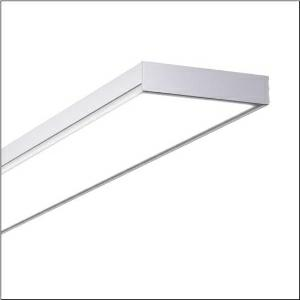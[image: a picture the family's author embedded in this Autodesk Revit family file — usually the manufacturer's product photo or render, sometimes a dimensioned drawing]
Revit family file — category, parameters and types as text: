
# Revit family: apollon_r__31_51mp25wd2341e_bc28
name_source: partatom
category: Lighting Fixtures
units: mm (PartAtom-declared; Revit-internal decimal feet)

## family parameters
Cut with Voids When Loaded = No
Host = Face
Light Source = No
Part Type = Normal
Room Calculation Point = No
Round Connector Dimension = Use Diameter
Shared = No

## types (1)
- Apollon® 31 (1 x LED, 3600 lm, 28 W, 3000K)
    Apparent Load = 28 VA
    CIE Flux Codes = 61 87 97 97 100
    Color Rendering = 80
    Color Temperature = 3000K
    Default Elevation = 1800 mm
    Description = Apollon® 31, office luminaire, primary optical cover: micro prismatic cover, of PMMA, light emission: direct distribution, primary light characteristic: symmetric, installation type: surface-mounted, LED, rated luminous flux: 3.600lm, luminous efficacy: 128lm/W, light colour: 830, colour temperature: 3000K, control gear: ECG DALI, with terminal, 5-pole, mains connection: 220..240V, AC, 50/60Hz, rated input power: 28W, housing, of sheet steel, coil coated, metallic grey (RAL 9006), length: 1.245mm, width: 200mm, height: 44mm, protection rating (complete): IP20, insulation class (complete): insulation class II (safety insulation), certification: CE, impact resistance: IK02, permissible operating ambient temperature: -20..+40°C, standard: EN 60598-2-22, packaging unit: 1 piece
    Height = 44 mm
    Lamp = 1 x LED
    Lamp Light Flux = 3600 lm
    Lamp Power = 28 W
    Lamp count = 1
    Length = 1245 mm
    Luminous efficacy = 129 lm/W
    Manufacturer = Siteco
    ModVariant = No
    Model = 51MP25WD2341E
    Mounting Place = Ceiling
    Mounting Type = Surface mounted
    Number of Poles = 1
    OnlyDefault = Yes
    Power Factor = 1
    Product Name = Apollon® 31
    Product group = office luminaire | ceiling mounted
    ProductGroupID = 302
    Protection Class = Protection class II
    Protection Degree = IP 20
    RLX_Detail_Level = 1
    RlxData = <blob elided: 24081 chars, md5=c3f55dd4>
    Socket = socket
    Standby Power = 0 W
    System Light Flux = 3600 lm
    System Power = 28 W
    Type Comments = Product without accessories
    Type Image = l_1007091.jpg
    URL = http://relux.com
    VarID = ---
    Voltage = 0 V
    Weight = 0.00 kg
    Width = 200 mm  [stored 0.656168 ft]

note: [stored X ft] marks values corroborated as IEEE doubles in the binary element streams (Revit-internal decimal feet)

## geometry (parser evidence)
native form markers: Blend x4, Sweep x10
no freeform markers — native parametric forms only
